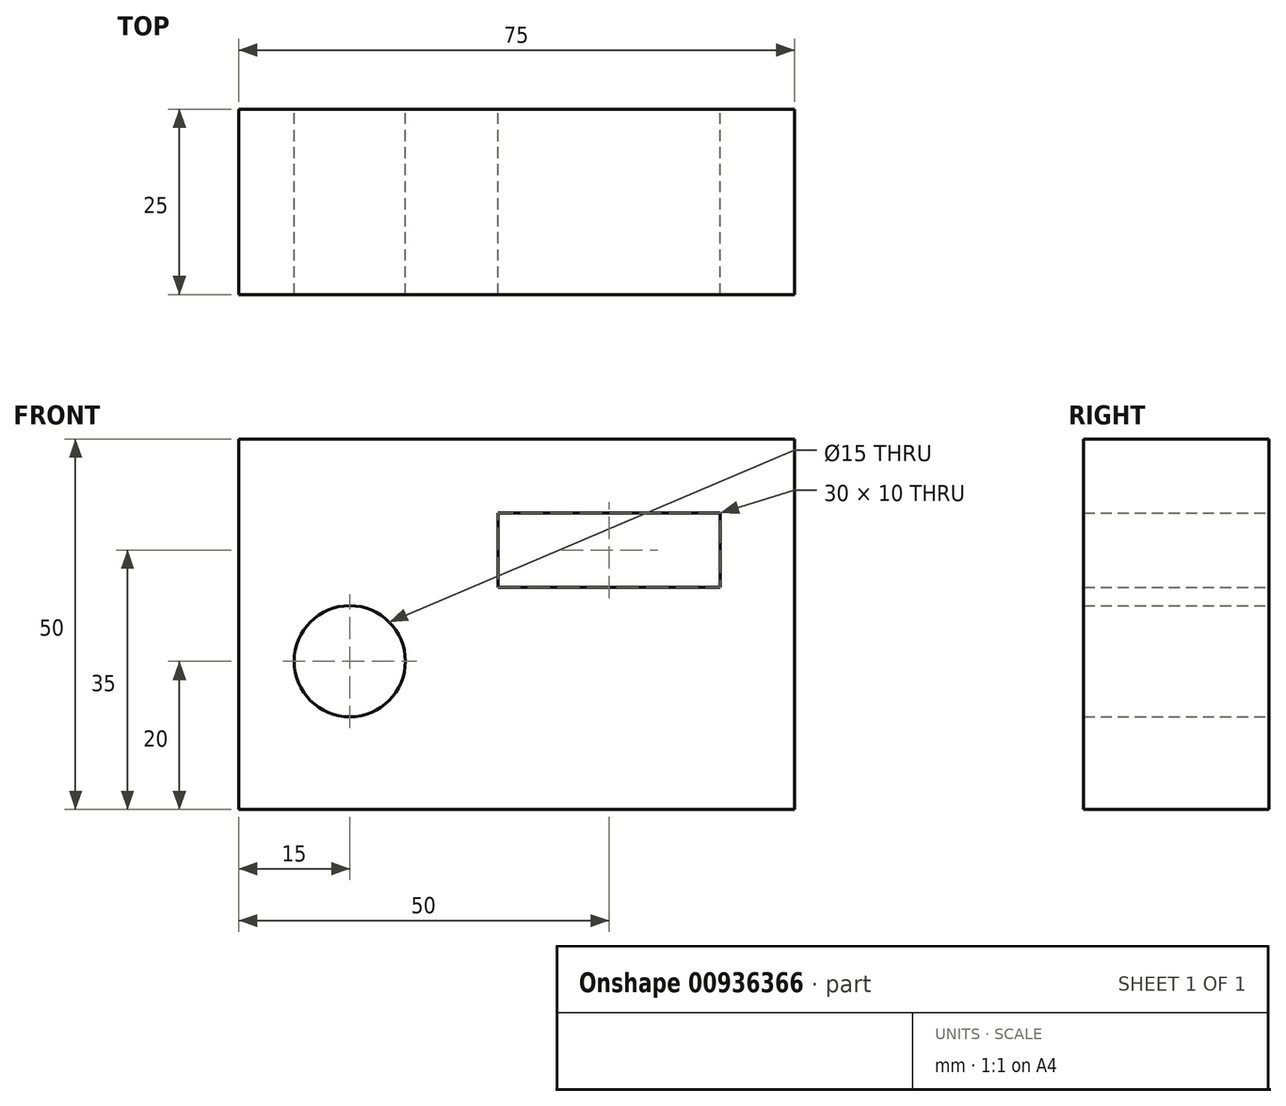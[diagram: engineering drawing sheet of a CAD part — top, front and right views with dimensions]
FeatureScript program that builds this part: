
annotation { "Feature Type Name" : "Feature", "Feature Type Description" : "" }
export const myFeature = defineFeature(function(context is Context, id is Id, definition is map)
    precondition{}
    {
        {
            var Q0;
            Q0=qCreatedBy(makeId("Front.planeOp"),FACE);
            var sketch = newSketch(context, id + "F0", { "sketchPlane" : qUnion([Q0])});
            skLineSegment(sketch, "E0.bottom", {"start": v(60, 30) * mm, "end": v(-15, 30) * mm});
            skLineSegment(sketch, "E0.top", {"start": v(60, -20) * mm, "end": v(-15, -20) * mm});
            skLineSegment(sketch, "E0.left", {"start": v(60, 30) * mm, "end": v(60, -20) * mm});
            skLineSegment(sketch, "E0.right", {"start": v(-15, 30) * mm, "end": v(-15, -20) * mm});
            skCircle(sketch, "E1", {"center": v(0, 0) * mm, "radius": 7.5 * mm});
            skLineSegment(sketch, "E2.bottom", {"start": v(20, 20) * mm, "end": v(50, 20) * mm});
            skLineSegment(sketch, "E2.top", {"start": v(20, 10) * mm, "end": v(50, 10) * mm});
            skLineSegment(sketch, "E2.left", {"start": v(20, 20) * mm, "end": v(20, 10) * mm});
            skLineSegment(sketch, "E2.right", {"start": v(50, 20) * mm, "end": v(50, 10) * mm});
            skPoint(sketch, "E2.middle", {"position": v(35, 15) * mm});
            skSolve(sketch);
        }
        {
            var Q0;
            Q0=makeQuery(id+"F0.imprint","IMPRINT",FACE,{"disambiguationData":[TD([[makeQuery(id+"F0.imprint","IMPRINT",EDGE,{"derivedFrom":sQuery(id+"F0.wireOp",EDGE,"E0.bottom")}),1.0]])]});
            extrude(context, id + "F1", {"entities" : qUnion([Q0]), "depth" : 25 * mm, "offsetDistance" : 25 * mm});
        }
    });
